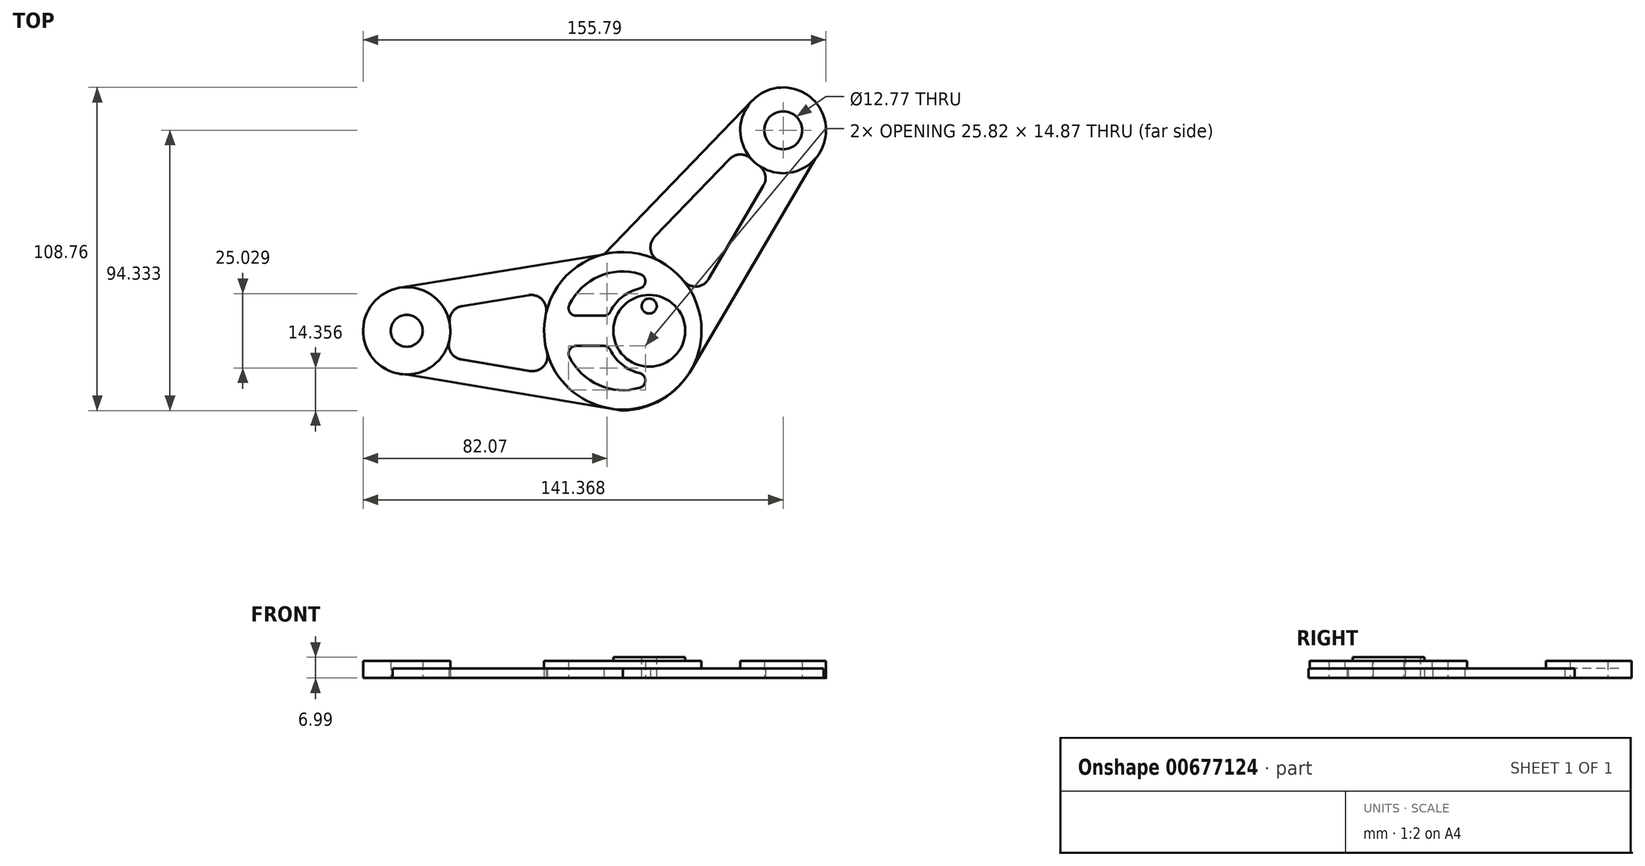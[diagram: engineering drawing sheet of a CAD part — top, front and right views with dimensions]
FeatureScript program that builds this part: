
annotation { "Feature Type Name" : "Feature", "Feature Type Description" : "" }
export const myFeature = defineFeature(function(context is Context, id is Id, definition is map)
    precondition{}
    {
        {
            var Q0;
            Q0=qCreatedBy(makeId("Top.planeOp"),FACE);
            var sketch = newSketch(context, id + "F0", { "sketchPlane" : qUnion([Q0])});
            skCircle(sketch, "E0", {"center": v(0, 0) * mm, "radius": 26.5 * mm, "construction": true});
            skCircle(sketch, "E1", {"center": v(-72.7, 0) * mm, "radius": 14.68 * mm, "construction": true});
            skCircle(sketch, "E2", {"center": v(53.98, 67.46) * mm, "radius": 14.42 * mm, "construction": true});
            skLineSegment(sketch, "E3", {"start": v(43.6, 77.48) * mm, "end": v(-6.36, 25.73) * mm});
            skLineSegment(sketch, "E4", {"start": v(-6.36, 25.73) * mm, "end": v(-75.08, 14.49) * mm});
            skLineSegment(sketch, "E5", {"start": v(67.55, 62.6) * mm, "end": v(22.84, -13.43) * mm});
            skLineSegment(sketch, "E6", {"start": v(-77.4, -13.9) * mm, "end": v(0, -26.87) * mm});
            skArc(sketch, "E7", {"start": v(-75.08, 14.49) * mm, "mid": v(-87.34, 1.2) * mm, "end": v(-77.4, -13.9) * mm});
            skArc(sketch, "E8", {"start": v(43.6, 77.48) * mm, "mid": v(61.6, 79.71) * mm, "end": v(67.55, 62.6) * mm});
            skArc(sketch, "E9", {"start": v(22.84, -13.43) * mm, "mid": v(13.16, -23.11) * mm, "end": v(0, -26.87) * mm});
            skLineSegment(sketch, "E10", {"start": v(-60, 7.35) * mm, "end": v(-22.85, 13.43) * mm});
            skLineSegment(sketch, "E11", {"start": v(-60.8, -8.58) * mm, "end": v(-21.76, -15.12) * mm});
            skLineSegment(sketch, "E12", {"start": v(40.47, 62.42) * mm, "end": v(5.28, 25.97) * mm});
            skLineSegment(sketch, "E13", {"start": v(50.55, 54.3) * mm, "end": v(24.53, 10.03) * mm});
            skArc(sketch, "E14", {"start": v(40.47, 62.42) * mm, "mid": v(44.23, 56.83) * mm, "end": v(50.13, 53.56) * mm});
            skArc(sketch, "E15", {"start": v(5.28, 25.97) * mm, "mid": v(16.9, 20.41) * mm, "end": v(24.53, 10.03) * mm});
            skArc(sketch, "E16", {"start": v(-22.85, 13.43) * mm, "mid": v(-26.48, -1) * mm, "end": v(-21.76, -15.12) * mm});
            skArc(sketch, "E17", {"start": v(-60, 7.35) * mm, "mid": v(-58.05, -0.73) * mm, "end": v(-60.8, -8.58) * mm});
            skSolve(sketch);
        }
        {
            var Q0;
            Q0 = qSketchRegion(id + "F0", true);
            extrude(context, id + "F1", {"entities" : qUnion([Q0]), "depth" : 3.17 * mm, "offsetDistance" : 25.4 * mm});
        }
        {
            var Q0;
            Q0=makeQuery(id+"F1.opExtrude","CAP_FACE",FACE,{"disambiguationData":[OSD([sQuery(id+"F0.wireOp",EDGE,"E3"),sQuery(id+"F0.wireOp",EDGE,"E4"),sQuery(id+"F0.wireOp",EDGE,"E5"),sQuery(id+"F0.wireOp",EDGE,"E6"),sQuery(id+"F0.wireOp",EDGE,"E7"),sQuery(id+"F0.wireOp",EDGE,"E8"),sQuery(id+"F0.wireOp",EDGE,"E9"),sQuery(id+"F0.wireOp",EDGE,"E10"),sQuery(id+"F0.wireOp",EDGE,"E11"),sQuery(id+"F0.wireOp",EDGE,"E12"),sQuery(id+"F0.wireOp",EDGE,"E13"),sQuery(id+"F0.wireOp",EDGE,"E14"),sQuery(id+"F0.wireOp",EDGE,"E15"),sQuery(id+"F0.wireOp",EDGE,"E16"),sQuery(id+"F0.wireOp",EDGE,"E17")])],"isStart":false});
            var sketch = newSketch(context, id + "F2", { "sketchPlane" : qUnion([Q0])});
            skCircle(sketch, "E18", {"center": v(-72.7, 0) * mm, "radius": 14.68 * mm});
            skCircle(sketch, "E19", {"center": v(53.98, 67.46) * mm, "radius": 14.42 * mm});
            skCircle(sketch, "E20", {"center": v(0, 0) * mm, "radius": 26.5 * mm});
            skSolve(sketch);
        }
        {
            var Q0;
            Q0 = qSketchRegion(id + "F2", true);
            extrude(context, id + "F3", {"entities" : qUnion([Q0]), "operationType" : NewBodyOperationType.ADD, "depth" : 2.54 * mm, "offsetDistance" : 25.4 * mm});
        }
        {
            var Q0;
            Q0=makeQuery(id+"F3.opExtrude","CAP_FACE",FACE,{"disambiguationData":[OSD([sQuery(id+"F2.wireOp",EDGE,"E20")])],"isStart":false});
            var sketch = newSketch(context, id + "F4", { "sketchPlane" : qUnion([Q0])});
            skCircle(sketch, "E21", {"center": v(8.9, 0) * mm, "radius": 12.08 * mm});
            skSolve(sketch);
        }
        {
            var Q0;
            Q0 = qSketchRegion(id + "F4", true);
            extrude(context, id + "F5", {"entities" : qUnion([Q0]), "operationType" : NewBodyOperationType.ADD, "depth" : 1.27 * mm, "offsetDistance" : 25.4 * mm});
        }
        {
            var Q0;
            Q0=makeQuery(id+"F5.opExtrude","CAP_FACE",FACE,{"disambiguationData":[OSD([sQuery(id+"F4.wireOp",EDGE,"E21")])],"isStart":false});
            var sketch = newSketch(context, id + "F6", { "sketchPlane" : qUnion([Q0])});
            skCircle(sketch, "E22", {"center": v(8.9, 8.33) * mm, "radius": 2.53 * mm});
            skPoint(sketch, "E23", {"position": v(8.9, 0) * mm});
            skLineSegment(sketch, "E24", {"start": v(8.9, 8.33) * mm, "end": v(8.9, 0) * mm, "construction": true});
            skSolve(sketch);
        }
        {
            var Q0;
            Q0 = qSketchRegion(id + "F6", true);
            extrude(context, id + "F7", {"entities" : qUnion([Q0]), "operationType" : NewBodyOperationType.REMOVE, "endBound" : BoundingType.THROUGH_ALL, "oppositeDirection" : true, "depth" : 25.4 * mm, "offsetDistance" : 25.4 * mm});
        }
        {
            var Q0;
            Q0=makeQuery(id+"F1.opExtrude","CAP_FACE",FACE,{"disambiguationData":[OSD([sQuery(id+"F0.wireOp",EDGE,"E3"),sQuery(id+"F0.wireOp",EDGE,"E4"),sQuery(id+"F0.wireOp",EDGE,"E5"),sQuery(id+"F0.wireOp",EDGE,"E6"),sQuery(id+"F0.wireOp",EDGE,"E7"),sQuery(id+"F0.wireOp",EDGE,"E8"),sQuery(id+"F0.wireOp",EDGE,"E9"),sQuery(id+"F0.wireOp",EDGE,"E10"),sQuery(id+"F0.wireOp",EDGE,"E11"),sQuery(id+"F0.wireOp",EDGE,"E12"),sQuery(id+"F0.wireOp",EDGE,"E13"),sQuery(id+"F0.wireOp",EDGE,"E14"),sQuery(id+"F0.wireOp",EDGE,"E15"),sQuery(id+"F0.wireOp",EDGE,"E16"),sQuery(id+"F0.wireOp",EDGE,"E17")])],"isStart":true});
            var sketch = newSketch(context, id + "F8", { "sketchPlane" : qUnion([Q0])});
            skCircle(sketch, "E25", {"center": v(0, 0) * mm, "radius": 19.98 * mm, "construction": true});
            skCircle(sketch, "E26", {"center": v(-72.7, 0) * mm, "radius": 5.37 * mm});
            skCircle(sketch, "E27", {"center": v(53.98, -67.46) * mm, "radius": 6.38 * mm});
            skArc(sketch, "E28", {"start": v(14.92, -13.3) * mm, "mid": v(-4.66, -19.43) * mm, "end": v(-19.33, -5.08) * mm});
            skArc(sketch, "E29", {"start": v(14.92, 13.3) * mm, "mid": v(-4.66, 19.43) * mm, "end": v(-19.33, 5.08) * mm});
            skCircle(sketch, "E30", {"center": v(8.9, 0) * mm, "radius": 12.08 * mm, "construction": true});
            skCircle(sketch, "E31", {"center": v(8.9, 0) * mm, "radius": 14.6 * mm, "construction": true});
            skLineSegment(sketch, "E32", {"start": v(-19.33, -5.08) * mm, "end": v(-4.78, -5.08) * mm});
            skLineSegment(sketch, "E33", {"start": v(-19.33, 5.08) * mm, "end": v(-4.78, 5.08) * mm});
            skArc(sketch, "E34", {"start": v(14.92, -13.3) * mm, "mid": v(3.28, -13.47) * mm, "end": v(-4.78, -5.08) * mm});
            skArc(sketch, "E35", {"start": v(-4.78, 5.08) * mm, "mid": v(3.28, 13.47) * mm, "end": v(14.92, 13.3) * mm});
            skSolve(sketch);
        }
        {
            var Q0;
            Q0 = qSketchRegion(id + "F8", true);
            extrude(context, id + "F9", {"entities" : qUnion([Q0]), "operationType" : NewBodyOperationType.REMOVE, "endBound" : BoundingType.THROUGH_ALL, "oppositeDirection" : true, "depth" : 25.4 * mm, "offsetDistance" : 25.4 * mm});
        }
        {
            var Q0;
            Q0=makeQuery(id+"F1.opExtrude","SWEPT_EDGE",EDGE,{"disambiguationData":[OSD([sQuery(id+"F0.wireOp",EDGE,"E12"),sQuery(id+"F0.wireOp",EDGE,"E14")])]});
            var Q1;
            Q1=makeQuery(id+"F1.opExtrude","SWEPT_EDGE",EDGE,{"disambiguationData":[OSD([sQuery(id+"F0.wireOp",EDGE,"E13"),sQuery(id+"F0.wireOp",EDGE,"E14")])]});
            var Q2;
            Q2=makeQuery(id+"F1.opExtrude","SWEPT_EDGE",EDGE,{"disambiguationData":[OSD([sQuery(id+"F0.wireOp",EDGE,"E12"),sQuery(id+"F0.wireOp",EDGE,"E15")])]});
            var Q3;
            Q3=makeQuery(id+"F1.opExtrude","SWEPT_EDGE",EDGE,{"disambiguationData":[OSD([sQuery(id+"F0.wireOp",EDGE,"E13"),sQuery(id+"F0.wireOp",EDGE,"E15")])]});
            var Q4;
            Q4=makeQuery(id+"F1.opExtrude","SWEPT_EDGE",EDGE,{"disambiguationData":[OSD([sQuery(id+"F0.wireOp",EDGE,"E10"),sQuery(id+"F0.wireOp",EDGE,"E17")])]});
            var Q5;
            Q5=makeQuery(id+"F1.opExtrude","SWEPT_EDGE",EDGE,{"disambiguationData":[OSD([sQuery(id+"F0.wireOp",EDGE,"E10"),sQuery(id+"F0.wireOp",EDGE,"E16")])]});
            var Q6;
            Q6=makeQuery(id+"F1.opExtrude","SWEPT_EDGE",EDGE,{"disambiguationData":[OSD([sQuery(id+"F0.wireOp",EDGE,"E11"),sQuery(id+"F0.wireOp",EDGE,"E17")])]});
            var Q7;
            Q7=makeQuery(id+"F1.opExtrude","SWEPT_EDGE",EDGE,{"disambiguationData":[OSD([sQuery(id+"F0.wireOp",EDGE,"E11"),sQuery(id+"F0.wireOp",EDGE,"E16")])]});
            fillet(context, id + "F10", {"entities" : qUnion([Q0, Q1, Q2, Q3, Q4, Q5, Q6, Q7]), "radius" : 5.08 * mm, "tangentPropagation" : true, "allowEdgeOverflow" : false});
        }
        {
            var Q0;
            Q0=makeQuery(id+"F9.boolean.opBoolean","COPY",EDGE,{"derivedFrom":makeQuery(id+"F9.opExtrude","SWEPT_EDGE",EDGE,{"disambiguationData":[OSD([sQuery(id+"F8.wireOp",EDGE,"E28"),sQuery(id+"F8.wireOp",EDGE,"E34")])]})});
            var Q1;
            Q1=makeQuery(id+"F9.boolean.opBoolean","COPY",EDGE,{"derivedFrom":makeQuery(id+"F9.opExtrude","SWEPT_EDGE",EDGE,{"disambiguationData":[OSD([sQuery(id+"F8.wireOp",EDGE,"E32"),sQuery(id+"F8.wireOp",EDGE,"E34")])]})});
            var Q2;
            Q2=makeQuery(id+"F9.boolean.opBoolean","COPY",EDGE,{"derivedFrom":makeQuery(id+"F9.opExtrude","SWEPT_EDGE",EDGE,{"disambiguationData":[OSD([sQuery(id+"F8.wireOp",EDGE,"E28"),sQuery(id+"F8.wireOp",EDGE,"E32")])]})});
            var Q3;
            Q3=makeQuery(id+"F9.boolean.opBoolean","COPY",EDGE,{"derivedFrom":makeQuery(id+"F9.opExtrude","SWEPT_EDGE",EDGE,{"disambiguationData":[OSD([sQuery(id+"F8.wireOp",EDGE,"E33"),sQuery(id+"F8.wireOp",EDGE,"E35")])]})});
            var Q4;
            Q4=makeQuery(id+"F9.boolean.opBoolean","COPY",EDGE,{"derivedFrom":makeQuery(id+"F9.opExtrude","SWEPT_EDGE",EDGE,{"disambiguationData":[OSD([sQuery(id+"F8.wireOp",EDGE,"E29"),sQuery(id+"F8.wireOp",EDGE,"E35")])]})});
            var Q5;
            Q5=makeQuery(id+"F9.boolean.opBoolean","COPY",EDGE,{"derivedFrom":makeQuery(id+"F9.opExtrude","SWEPT_EDGE",EDGE,{"disambiguationData":[OSD([sQuery(id+"F8.wireOp",EDGE,"E29"),sQuery(id+"F8.wireOp",EDGE,"E33")])]})});
            fillet(context, id + "F11", {"entities" : qUnion([Q0, Q1, Q2, Q3, Q4, Q5]), "radius" : 2.54 * mm, "tangentPropagation" : true, "allowEdgeOverflow" : false});
        }
        {
            var Q0;
            Q0=sQuery(id+"F6.wireOp",VERTEX,"E23");
            var Q1;
            Q1=qCreatedBy(makeId("Right.planeOp"),FACE);
            cPlane(context, id + "F12", {"entities" : qUnion([Q0, Q1]), "cplaneType" : CPlaneType.PLANE_POINT, "offset" : 25.4 * mm, "width" : 152.4 * mm, "height" : 152.4 * mm});
        }
        {
            var Q0;
            Q0=qCreatedBy(id+"F12.planeOp",FACE);
            var sketch = newSketch(context, id + "F13", { "sketchPlane" : qUnion([Q0])});
            skLineSegment(sketch, "E36", {"start": v(0, 7.26) * mm, "end": v(0, 0) * mm});
            skSolve(sketch);
        }
    });
